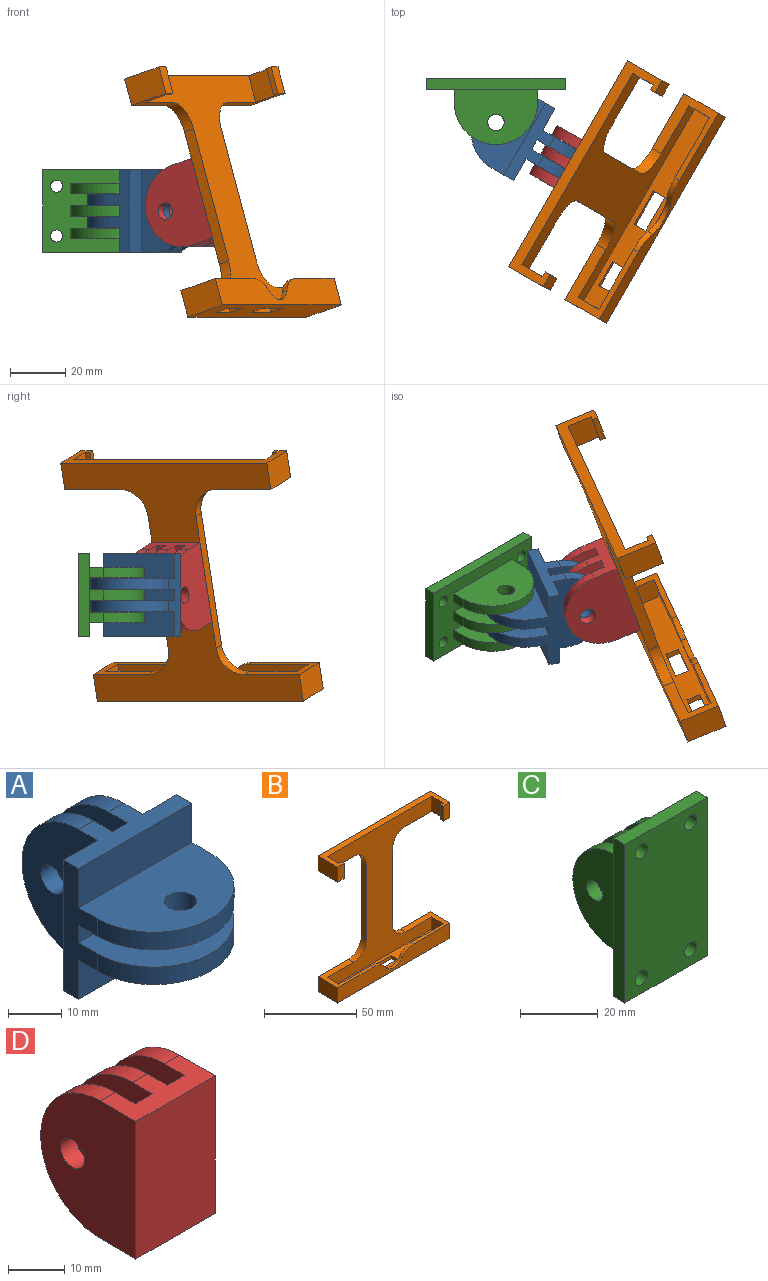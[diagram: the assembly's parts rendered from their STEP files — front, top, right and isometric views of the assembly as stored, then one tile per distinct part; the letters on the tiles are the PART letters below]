
ASSEMBLY  parts=4 mates=3
PART A: 26 faces, bbox 30x44x30 mm
  f0: plane 30x20mm, normal (0,0,1), area 475.2mm2, adj f5,f12,f14,f23,f25
  f1: plane 30x20mm, normal (0,0,-1), area 475.2mm2, adj f4,f12,f14,f23,f25
  f2: plane 30x20mm, normal (0,0,-1), area 475.2mm2, adj f12,f14,f15,f22,f24
  f3: plane 30x20mm, normal (0,0,1), area 475.2mm2, adj f4,f12,f14,f22,f24
  f4: plane 30x4mm, normal (0,-1,0), area 120mm2, adj f1,f3,f12,f14
  f5: plane 30x9mm, normal (0,-1,0), area 270mm2, adj f0,f12,f13,f14
  f6: plane 30x20mm, normal (1,0,0), area 475.2mm2, adj f9,f11,f13,f19,f21
  f7: plane 30x20mm, normal (-1,0,0), area 475.2mm2, adj f9,f11,f13,f18,f20
  f8: plane 30x20mm, normal (1,0,0), area 475.2mm2, adj f11,f13,f16,f18,f20
  f9: plane 30x4mm, normal (0,1,0), area 120mm2, adj f6,f7,f11,f13
  f10: plane 30x9mm, normal (0,1,0), area 270mm2, adj f11,f13,f14,f17
  f11: plane 30x9mm, normal (0,0,-1), area 160mm2, adj f6,f7,f8,f9,f10,f12,f14,f15
  f12: plane 30x9mm, normal (1,0,0), area 160mm2, adj f0,f1,f2,f3,f4,f5,f11,f13
  f13: plane 30x9mm, normal (0,0,1), area 160mm2, adj f5,f6,f7,f8,f9,f10,f12,f14
  f14: plane 30x9mm, normal (-1,0,0), area 160mm2, adj f0,f1,f2,f3,f4,f5,f10,f11
  f15: plane 30x9mm, normal (0,-1,0), area 270mm2, adj f2,f11,f12,f14
  f16: plane 30x9mm, normal (0,1,0), area 270mm2, adj f8,f11,f12,f13
  f17: plane 30x20mm, normal (-1,0,0), area 475.2mm2, adj f10,f11,f13,f19,f21
  f18: cylinder r=15mm len=30mm, axis (-1,0,0), area 188.5mm2, adj f7,f8,f11,f13
  f19: cylinder r=15mm len=30mm, axis (-1,0,0), area 188.5mm2, adj f6,f11,f13,f17
  f20: cylinder r=3mm len=6mm, axis (-1,0,0), area 75.4mm2, adj f7,f8
  f21: cylinder r=3mm len=6mm, axis (-1,0,0), area 75.4mm2, adj f6,f17
  f22: cylinder r=15mm len=30mm, axis (0,0,1), area 188.5mm2, adj f2,f3,f12,f14
  f23: cylinder r=15mm len=30mm, axis (0,0,1), area 188.5mm2, adj f0,f1,f12,f14
  f24: cylinder r=3mm len=6mm, axis (0,0,1), area 75.4mm2, adj f2,f3
  f25: cylinder r=3mm len=6mm, axis (0,0,1), area 75.4mm2, adj f0,f1
PART B: 43 faces, bbox 86x15x90 mm
  f0: plane 28.03x15mm, normal (0,0,1), area 175.1mm2, adj f1,f2,f3,f9,f15,f21,f29,f39
  f1: plane 40x8mm, normal (0,1,0), area 262.8mm2, adj f0,f3,f19,f22,f29
  f2: plane 88x80mm, normal (0,-1,0), area 2925.8mm2, adj f0,f3,f4,f5,f6,f8,f10,f11
  f3: plane 9x8mm, normal (1,0,0), area 72mm2, adj f0,f1,f2,f19
  f4: plane 9x8mm, normal (-1,0,0), area 72mm2, adj f2,f12,f19,f20
  f5: plane 50x4mm, normal (1,0,0), area 200mm2, adj f2,f9,f40,f41
  f6: plane 50x4mm, normal (-1,0,0), area 200mm2, adj f2,f9,f39,f42
  f7: plane 86x15mm, normal (0,0,-1), area 1170mm2, adj f9,f15,f18,f21,f31,f32,f33,f34
  f8: plane 86x15mm, normal (0,0,1), area 418mm2, adj f2,f9,f13,f14,f16,f17,f23,f24
  f9: plane 90x86mm, normal (0,1,0), area 3205.8mm2, adj f0,f5,f6,f7,f8,f10,f11,f12
  f10: plane 23x15mm, normal (0,0,-1), area 129mm2, adj f2,f9,f13,f14,f23,f24,f25,f42
  f11: plane 23x15mm, normal (0,0,-1), area 129mm2, adj f2,f9,f16,f17,f26,f27,f28,f41
  f12: plane 28.03x15mm, normal (0,0,1), area 175.1mm2, adj f2,f4,f9,f18,f20,f21,f30,f40
  f13: plane 15x10mm, normal (-1,0,0), area 150mm2, adj f8,f9,f10,f24
  f14: plane 10x9mm, normal (1,0,0), area 90mm2, adj f2,f8,f10,f25
  f15: plane 15x10mm, normal (-1,0,0), area 150mm2, adj f0,f7,f9,f21
  f16: plane 10x9mm, normal (-1,0,0), area 90mm2, adj f2,f8,f11,f26
  f17: plane 15x10mm, normal (1,0,0), area 150mm2, adj f8,f9,f11,f28
  f18: plane 15x10mm, normal (1,0,0), area 150mm2, adj f7,f9,f12,f21
  f19: plane 80x9mm, normal (0,0,1), area 600mm2, adj f1,f2,f3,f4,f20,f31,f32,f33
  f20: plane 40x8mm, normal (0,1,0), area 262.8mm2, adj f4,f12,f19,f22,f30
  f21: plane 86x10mm, normal (0,-1,0), area 745.7mm2, adj f0,f7,f12,f15,f18,f22,f29,f30
  f22: cylinder r=8mm len=13.3mm, axis (0,-1,0), area 31.4mm2, adj f1,f20,f21,f29,f30
  f23: plane 10x2mm, normal (1,0,0), area 20mm2, adj f8,f10,f24,f25
  f24: plane 10x5mm, normal (0,-1,0), area 50mm2, adj f8,f10,f13,f23
  f25: plane 10x2mm, normal (0,1,0), area 20mm2, adj f8,f10,f14,f23
  f26: plane 10x2mm, normal (0,1,0), area 20mm2, adj f8,f11,f16,f27
  f27: plane 10x2mm, normal (-1,0,0), area 20mm2, adj f8,f11,f26,f28
  f28: plane 10x5mm, normal (0,-1,0), area 50mm2, adj f8,f11,f17,f27
  f29: cylinder r=10mm len=8.31mm, axis (0,-1,0), area 19.6mm2, adj f0,f1,f21,f22
  f30: cylinder r=10mm len=8.31mm, axis (0,-1,0), area 19.6mm2, adj f12,f20,f21,f22
  f31: plane 5x2mm, normal (1,0,0), area 10mm2, adj f7,f19,f32,f34
  f32: plane 10x2mm, normal (0,1,0), area 20mm2, adj f7,f19,f31,f33
  f33: plane 5x2mm, normal (-1,0,0), area 10mm2, adj f7,f19,f32,f34
  f34: plane 10x2mm, normal (0,-1,0), area 20mm2, adj f7,f19,f31,f33
  f35: plane 5x2mm, normal (1,0,0), area 10mm2, adj f7,f19,f36,f38
  f36: plane 14x2mm, normal (0,1,0), area 28mm2, adj f7,f19,f35,f37
  f37: plane 5x2mm, normal (-1,0,0), area 10mm2, adj f7,f19,f36,f38
  f38: plane 14x2mm, normal (0,-1,0), area 28mm2, adj f7,f19,f35,f37
  f39: cylinder r=10mm len=10mm, axis (0,-1,0), area 62.8mm2, adj f0,f2,f6,f9
  f40: cylinder r=10mm len=10mm, axis (0,1,0), area 62.8mm2, adj f2,f5,f9,f12
  f41: cylinder r=10mm len=10mm, axis (0,1,0), area 62.8mm2, adj f2,f5,f9,f11
  f42: cylinder r=10mm len=10mm, axis (0,1,0), area 62.8mm2, adj f2,f6,f9,f10
PART C: 28 faces, bbox 30x24x50 mm
  f0: plane 30x20mm, normal (-1,0,0), area 475.2mm2, adj f1,f5,f12,f14,f17
  f1: plane 5x3.8mm, normal (0,0,-1), area 19mm2, adj f0,f9,f12,f14
  f2: plane 5x3.8mm, normal (0,0,-1), area 19mm2, adj f10,f11,f12,f13
  f3: plane 5x3.8mm, normal (0,0,-1), area 19mm2, adj f4,f8,f12,f15
  f4: plane 30x20mm, normal (1,0,0), area 475.2mm2, adj f3,f7,f12,f15,f18
  f5: plane 5x3.8mm, normal (0,0,1), area 19mm2, adj f0,f9,f12,f14
  f6: plane 5x3.8mm, normal (0,0,1), area 19mm2, adj f10,f11,f12,f13
  f7: plane 5x3.8mm, normal (0,0,1), area 19mm2, adj f4,f8,f12,f15
  f8: plane 30x20mm, normal (-1,0,0), area 475.2mm2, adj f3,f7,f12,f15,f18
  f9: plane 30x20mm, normal (1,0,0), area 475.2mm2, adj f1,f5,f12,f14,f17
  f10: plane 30x20mm, normal (-1,0,0), area 475.2mm2, adj f2,f6,f12,f13,f16
  f11: plane 30x20mm, normal (1,0,0), area 475.2mm2, adj f2,f6,f12,f13,f16
  f12: plane 50x30mm, normal (0,1,0), area 1097.2mm2, adj f0,f1,f2,f3,f4,f5,f6,f7
  f13: cylinder r=15mm len=30mm, axis (1,0,0), area 179.1mm2, adj f2,f6,f10,f11
  f14: cylinder r=15mm len=30mm, axis (1,0,0), area 179.1mm2, adj f0,f1,f5,f9
  f15: cylinder r=15mm len=30mm, axis (1,0,0), area 179.1mm2, adj f3,f4,f7,f8
  f16: cylinder r=3mm len=6mm, axis (1,0,0), area 71.6mm2, adj f10,f11
  f17: cylinder r=3mm len=6mm, axis (1,0,0), area 71.6mm2, adj f0,f9
  f18: cylinder r=3mm len=6mm, axis (1,0,0), area 71.6mm2, adj f4,f8
  f19: plane 50x4mm, normal (-1,0,0), area 200mm2, adj f12,f20,f22,f23
  f20: plane 30x4mm, normal (0,0,-1), area 120mm2, adj f12,f19,f21,f23
  f21: plane 50x4mm, normal (1,0,0), area 200mm2, adj f12,f20,f22,f23
  f22: plane 30x4mm, normal (0,0,1), area 120mm2, adj f12,f19,f21,f23
  f23: plane 50x30mm, normal (0,-1,0), area 1439.2mm2, adj f19,f20,f21,f22,f24,f25,f26,f27
  f24: cylinder r=2.2mm len=4.4mm, axis (0,1,0), area 55.3mm2, adj f12,f23
  f25: cylinder r=2.2mm len=4.4mm, axis (0,1,0), area 55.3mm2, adj f12,f23
  f26: cylinder r=2.2mm len=4.4mm, axis (0,1,0), area 55.3mm2, adj f12,f23
  f27: cylinder r=2.2mm len=4.4mm, axis (0,1,0), area 55.3mm2, adj f12,f23
PART D: 17 faces, bbox 20x24x30 mm
  f0: plane 30x24mm, normal (-1,0,0), area 595.2mm2, adj f7,f9,f10,f12,f15
  f1: plane 30x20mm, normal (-1,0,0), area 475.2mm2, adj f5,f7,f9,f13,f16
  f2: plane 30x20mm, normal (1,0,0), area 475.2mm2, adj f6,f7,f9,f12,f15
  f3: plane 30x20mm, normal (-1,0,0), area 475.2mm2, adj f6,f7,f9,f11,f14
  f4: plane 30x20mm, normal (1,0,0), area 475.2mm2, adj f5,f7,f9,f11,f14
  f5: plane 30x4.3mm, normal (0,1,0), area 129mm2, adj f1,f4,f7,f9
  f6: plane 30x4.3mm, normal (0,1,0), area 129mm2, adj f2,f3,f7,f9
  f7: plane 20x9mm, normal (0,0,-1), area 137mm2, adj f0,f1,f2,f3,f4,f5,f6,f8
  f8: plane 30x24mm, normal (1,0,0), area 595.2mm2, adj f7,f9,f10,f13,f16
  f9: plane 20x9mm, normal (0,0,1), area 137mm2, adj f0,f1,f2,f3,f4,f5,f6,f8
  f10: plane 30x20mm, normal (0,-1,0), area 600mm2, adj f0,f7,f8,f9
  f11: cylinder r=15mm len=30mm, axis (1,0,0), area 179.1mm2, adj f3,f4,f7,f9
  f12: cylinder r=15mm len=30mm, axis (1,0,0), area 179.1mm2, adj f0,f2,f7,f9
  f13: cylinder r=15mm len=30mm, axis (1,0,0), area 179.1mm2, adj f1,f7,f8,f9
  f14: cylinder r=3mm len=6mm, axis (1,0,0), area 71.6mm2, adj f3,f4
  f15: cylinder r=3mm len=6mm, axis (1,0,0), area 71.6mm2, adj f0,f2
  f16: cylinder r=3mm len=6mm, axis (1,0,0), area 71.6mm2, adj f1,f8
PLACE A rot(axis=(0,0,-1),120deg) t=(4.08,42.35,0.29)mm
PLACE B rot(axis=(-0.25,-0.14,0.96),62.2deg) t=(27.77,28.79,4.98)mm
PLACE C rot(axis=(-0.71,0,0.71),180deg) t=(-9.77,66.35,0.29)mm fixed
PLACE D rot(axis=(-0.25,-0.14,0.96),62.2deg) t=(27.77,28.79,4.98)mm
MATE fastened D.f10 <-> B.f9  axis (0.83,-0.48,0.29) through (27.77,28.79,4.98)mm
MATE revolute C.f16 <-> A.f24  axis (0,0,-1) through (-9.77,50.35,6.29)mm
MATE revolute A.f20 <-> D.f14  axis (-0.5,-0.87,0) through (11.43,31.07,0.29)mm
